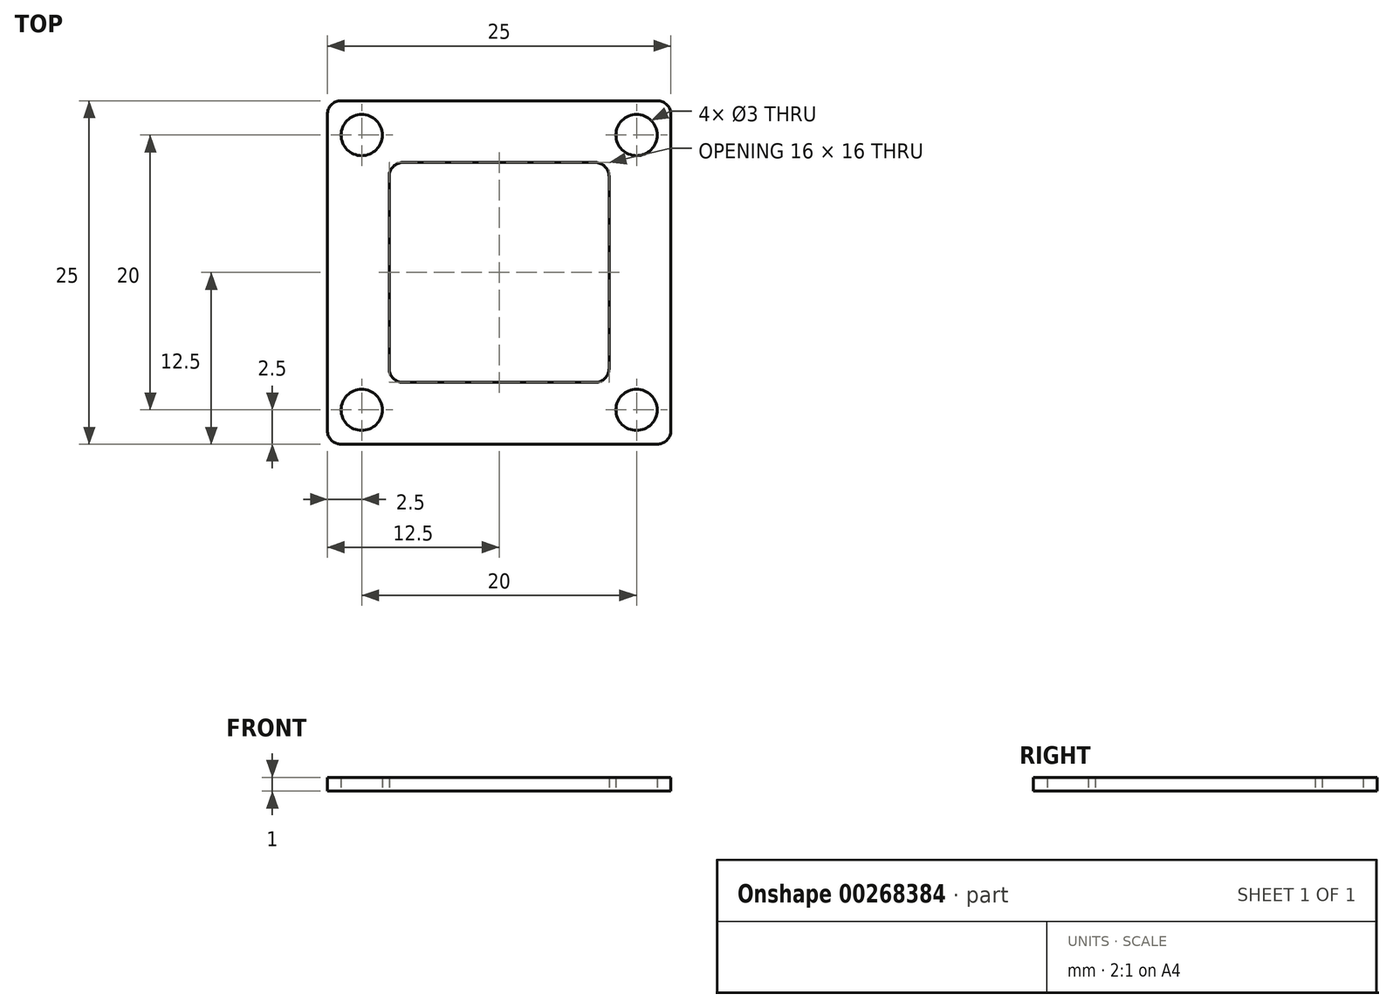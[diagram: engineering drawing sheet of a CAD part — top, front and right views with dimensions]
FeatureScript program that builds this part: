
annotation { "Feature Type Name" : "Feature", "Feature Type Description" : "" }
export const myFeature = defineFeature(function(context is Context, id is Id, definition is map)
    precondition{}
    {
        {
            var Q0;
            Q0=qCreatedBy(makeId("Top.planeOp"),FACE);
            var sketch = newSketch(context, id + "F0", { "sketchPlane" : qUnion([Q0])});
            skLineSegment(sketch, "E0.bottom", {"start": v(12.5, -12.5) * mm, "end": v(-12.5, -12.5) * mm});
            skLineSegment(sketch, "E0.top", {"start": v(12.5, 12.5) * mm, "end": v(-12.5, 12.5) * mm});
            skLineSegment(sketch, "E0.left", {"start": v(12.5, -12.5) * mm, "end": v(12.5, 12.5) * mm});
            skLineSegment(sketch, "E0.right", {"start": v(-12.5, -12.5) * mm, "end": v(-12.5, 12.5) * mm});
            skPoint(sketch, "E0.middle", {"position": v(0, 0) * mm});
            skCircle(sketch, "E1", {"center": v(-10, 10) * mm, "radius": 1.5 * mm});
            skCircle(sketch, "E2.0.1.0", {"center": v(-10, -10) * mm, "radius": 1.5 * mm});
            skCircle(sketch, "E2.1.0.0", {"center": v(10, 10) * mm, "radius": 1.5 * mm});
            skCircle(sketch, "E2.1.1.0", {"center": v(10, -10) * mm, "radius": 1.5 * mm});
            skLineSegment(sketch, "E2.direction1", {"start": v(-10, 10) * mm, "end": v(10, 10) * mm, "construction": true});
            skLineSegment(sketch, "E2.direction2", {"start": v(-10, 10) * mm, "end": v(-10, -10) * mm, "construction": true});
            skLineSegment(sketch, "E3", {"start": v(10, -10) * mm, "end": v(-10, 10) * mm, "construction": true});
            skLineSegment(sketch, "E4", {"start": v(-10, -10) * mm, "end": v(0, 0) * mm, "construction": true});
            skLineSegment(sketch, "E5.bottom", {"start": v(8, -8) * mm, "end": v(-8, -8) * mm});
            skLineSegment(sketch, "E5.top", {"start": v(8, 8) * mm, "end": v(-8, 8) * mm});
            skLineSegment(sketch, "E5.left", {"start": v(8, -8) * mm, "end": v(8, 8) * mm});
            skLineSegment(sketch, "E5.right", {"start": v(-8, -8) * mm, "end": v(-8, 8) * mm});
            skSolve(sketch);
        }
        {
            var Q0;
            Q0 = qSketchRegion(id + "F0", true);
            extrude(context, id + "F1", {"entities" : qUnion([Q0]), "depth" : 1 * mm});
        }
        {
            var Q0;
            Q0=makeQuery(id+"F1.opExtrude","SWEPT_EDGE",EDGE,{"disambiguationData":[OSD([sQuery(id+"F0.wireOp",EDGE,"E0.top"),sQuery(id+"F0.wireOp",EDGE,"E0.left")])]});
            var Q1;
            Q1=makeQuery(id+"F1.opExtrude","SWEPT_EDGE",EDGE,{"disambiguationData":[OSD([sQuery(id+"F0.wireOp",EDGE,"E0.bottom"),sQuery(id+"F0.wireOp",EDGE,"E0.left")])]});
            var Q2;
            Q2=makeQuery(id+"F1.opExtrude","SWEPT_EDGE",EDGE,{"disambiguationData":[OSD([sQuery(id+"F0.wireOp",EDGE,"E0.top"),sQuery(id+"F0.wireOp",EDGE,"E0.right")])]});
            var Q3;
            Q3=makeQuery(id+"F1.opExtrude","SWEPT_EDGE",EDGE,{"disambiguationData":[OSD([sQuery(id+"F0.wireOp",EDGE,"E0.bottom"),sQuery(id+"F0.wireOp",EDGE,"E0.right")])]});
            var Q4;
            Q4=makeQuery(id+"F1.opExtrude","SWEPT_EDGE",EDGE,{"disambiguationData":[OSD([sQuery(id+"F0.wireOp",EDGE,"E5.top"),sQuery(id+"F0.wireOp",EDGE,"E5.right")])]});
            var Q5;
            Q5=makeQuery(id+"F1.opExtrude","SWEPT_EDGE",EDGE,{"disambiguationData":[OSD([sQuery(id+"F0.wireOp",EDGE,"E5.bottom"),sQuery(id+"F0.wireOp",EDGE,"E5.right")])]});
            var Q6;
            Q6=makeQuery(id+"F1.opExtrude","SWEPT_EDGE",EDGE,{"disambiguationData":[OSD([sQuery(id+"F0.wireOp",EDGE,"E5.bottom"),sQuery(id+"F0.wireOp",EDGE,"E5.left")])]});
            var Q7;
            Q7=makeQuery(id+"F1.opExtrude","SWEPT_EDGE",EDGE,{"disambiguationData":[OSD([sQuery(id+"F0.wireOp",EDGE,"E5.top"),sQuery(id+"F0.wireOp",EDGE,"E5.left")])]});
            fillet(context, id + "F2", {"entities" : qUnion([Q0, Q1, Q2, Q3, Q4, Q5, Q6, Q7]), "radius" : 1 * mm, "tangentPropagation" : true, "allowEdgeOverflow" : false});
        }
    });
